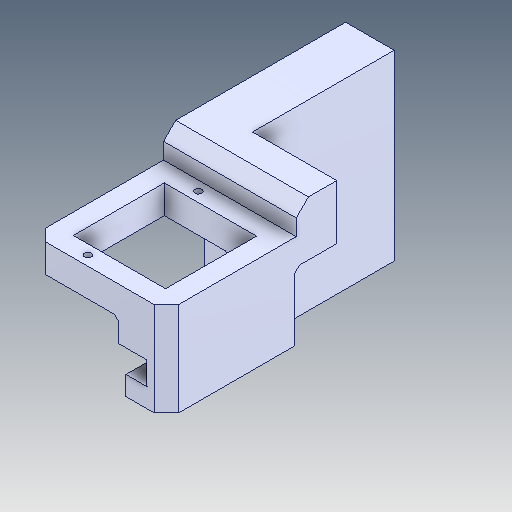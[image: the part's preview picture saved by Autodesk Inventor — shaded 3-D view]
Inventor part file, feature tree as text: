
AUTODESK INVENTOR PART (.ipt)
format: ipt  version: 2020 (Build 240168000, 168)  size: 140,800 bytes
history: mixed  units: mm
features: extrude x2, sketch x2, other x1, imported_body x1
ambient origin geometry x8: Origin, YZ Plane, XZ Plane, XY Plane, X Axis, Y Axis, Z Axis, Center Point
bodies: Solid1 (imported_parasolid)
feature tree (6):
  extrude  "Extrusion1"  Depth=24.0mm TaperAngle=0.0deg
  extrude  "Extrusion2"  [1 undecoded]
  sketch  "Sketch1"  dims[d0=25.0mm d1=0.0mm d2=24.0mm d3=0.0mm]
  sketch  "Sketch2"
  other  "Cut-Extrude3"
  imported_body  NMx_Import_Brep_tag  [imported B-rep: ~40 faces, bbox_mm=[32.8, 45.14, 77.1]]
note: 1 required parameter value undecoded (feature->parameter linkage not recoverable at this tier; creation-order binding heuristic only, values carry confidence <= 0.55)
